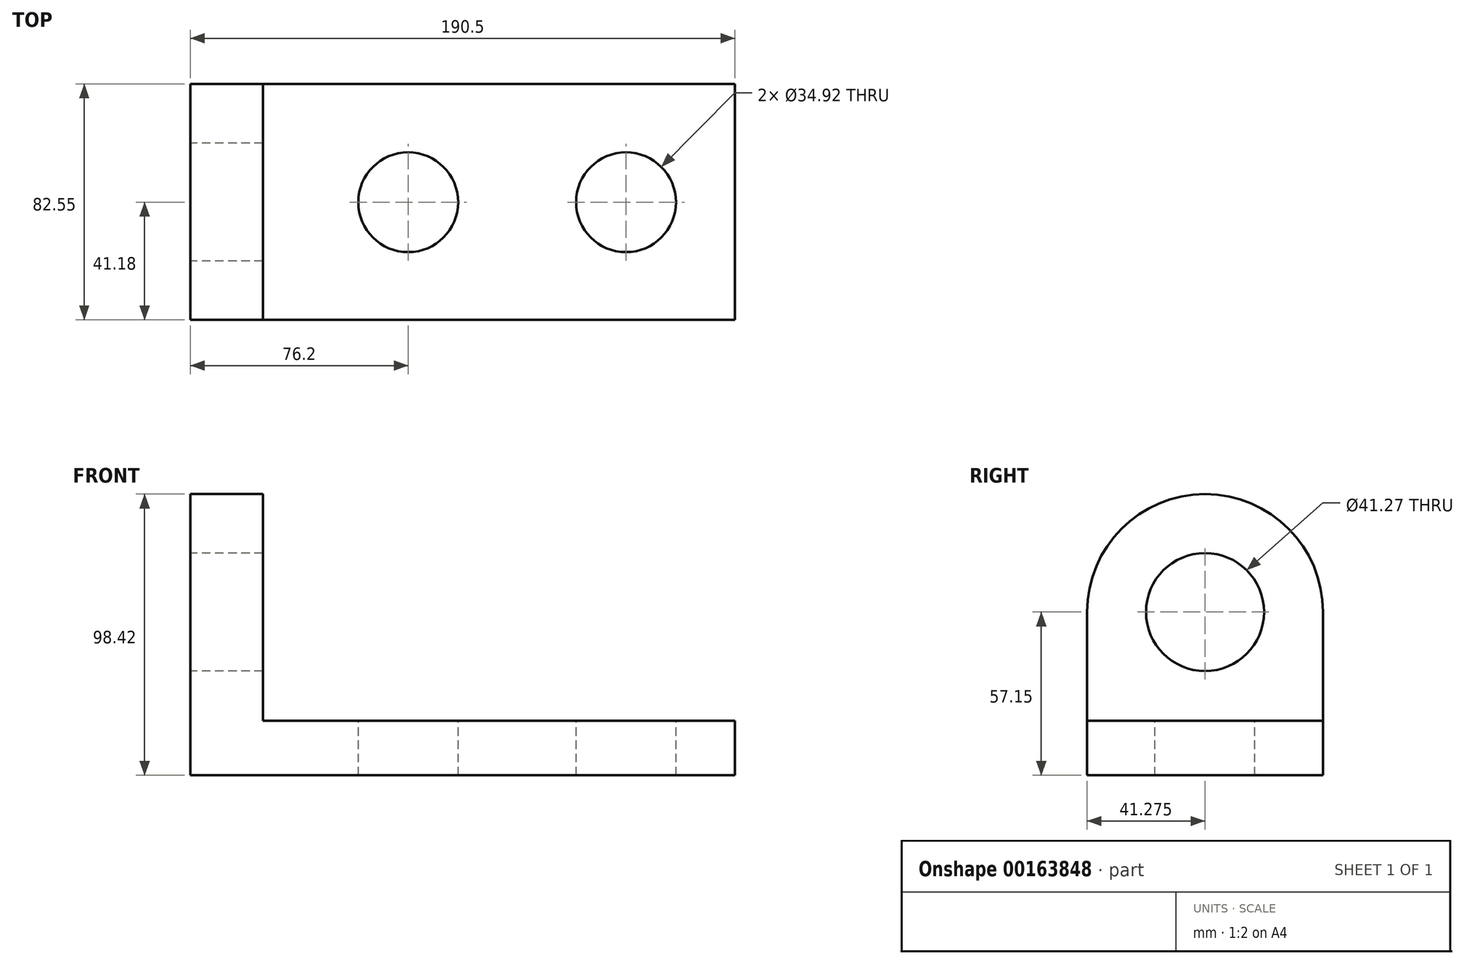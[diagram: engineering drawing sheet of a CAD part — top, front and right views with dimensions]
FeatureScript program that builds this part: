
annotation { "Feature Type Name" : "Feature", "Feature Type Description" : "" }
export const myFeature = defineFeature(function(context is Context, id is Id, definition is map)
    precondition{}
    {
        {
            var Q0;
            Q0=qCreatedBy(makeId("Right.planeOp"),FACE);
            var sketch = newSketch(context, id + "F0", { "sketchPlane" : qUnion([Q0])});
            skLineSegment(sketch, "E0", {"start": v(0, 0) * mm, "end": v(82.55, 0) * mm});
            skLineSegment(sketch, "E1", {"start": v(0, 0) * mm, "end": v(0, 19.05) * mm});
            skLineSegment(sketch, "E2", {"start": v(0, 19.05) * mm, "end": v(82.55, 19.05) * mm});
            skLineSegment(sketch, "E3", {"start": v(82.55, 19.05) * mm, "end": v(82.55, 0) * mm});
            skLineSegment(sketch, "E4", {"start": v(0, 0) * mm, "end": v(0, 57.15) * mm});
            skLineSegment(sketch, "E5", {"start": v(82.55, 0) * mm, "end": v(82.55, 57.15) * mm});
            skArc(sketch, "E6", {"start": v(82.55, 57.15) * mm, "mid": v(41.27, 98.43) * mm, "end": v(0, 57.15) * mm});
            skCircle(sketch, "E7", {"center": v(41.27, 57.15) * mm, "radius": 20.64 * mm});
            skSolve(sketch);
        }
        {
            var Q0;
            {var subQ2=sQuery(id+"F0.wireOp",EDGE,"E2");Q0=makeQuery(id+"F0.imprint","IMPRINT",FACE,{"disambiguationData":[TD([[makeQuery(id+"F0.imprint","IMPRINT",EDGE,{"derivedFrom":subQ2}),1.0]])]});}
            extrude(context, id + "F1", {"entities" : qUnion([Q0]), "depth" : 25.4 * mm});
        }
        {
            var Q0;
            {var subQ0=sQuery(id+"F0.wireOp",EDGE,"E0");Q0=makeQuery(id+"F0.imprint","IMPRINT",FACE,{"disambiguationData":[TD([[makeQuery(id+"F0.imprint","IMPRINT",EDGE,{"derivedFrom":subQ0}),1.0]])]});}
            extrude(context, id + "F2", {"entities" : qUnion([Q0]), "operationType" : NewBodyOperationType.ADD, "depth" : 190.5 * mm});
        }
        {
            var Q0;
            Q0=makeQuery(id+"F2.opExtrude","SWEPT_FACE",FACE,{"disambiguationData":[OSD([sQuery(id+"F0.wireOp",EDGE,"E2")])]});
            var sketch = newSketch(context, id + "F3", { "sketchPlane" : qUnion([Q0])});
            skLineSegment(sketch, "E8", {"start": v(190.5, 82.55) * mm, "end": v(152.4, 82.55) * mm});
            skCircle(sketch, "E9", {"center": v(152.4, 41.18) * mm, "radius": 17.46 * mm});
            skCircle(sketch, "E10", {"center": v(76.2, 41.18) * mm, "radius": 17.46 * mm});
            skSolve(sketch);
        }
        {
            var Q0;
            Q0=makeQuery(id+"F3.imprint","IMPRINT",FACE,{"disambiguationData":[TD([[makeQuery(id+"F3.imprint","IMPRINT",EDGE,{"derivedFrom":sQuery(id+"F3.wireOp",EDGE,"E10")}),1.0]])]});
            var Q1;
            Q1=makeQuery(id+"F3.imprint","IMPRINT",FACE,{"disambiguationData":[TD([[makeQuery(id+"F3.imprint","IMPRINT",EDGE,{"derivedFrom":sQuery(id+"F3.wireOp",EDGE,"E9")}),1.0]])]});
            extrude(context, id + "F4", {"entities" : qUnion([Q0, Q1]), "operationType" : NewBodyOperationType.REMOVE, "oppositeDirection" : true, "depth" : 25.4 * mm});
        }
    });
